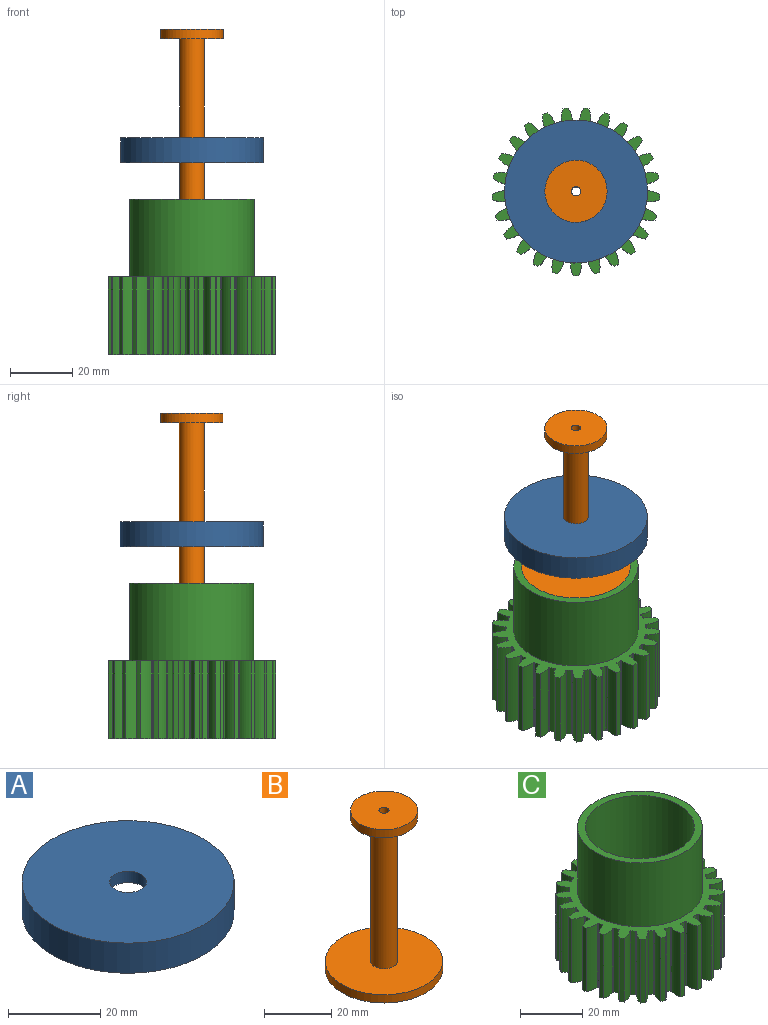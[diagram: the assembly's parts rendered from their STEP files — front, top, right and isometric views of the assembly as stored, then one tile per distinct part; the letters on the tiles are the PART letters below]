
ASSEMBLY  parts=3 mates=3
PART A: 6 faces, bbox 46x46x8 mm
  f0: cylinder r=4mm len=8mm, axis (0,0,1), area 75.4mm2, adj f1,f2
  f1: plane 40x40mm, normal (0,0,-1), area 1206.4mm2, adj f0,f3
  f2: plane 46x46mm, normal (0,0,1), area 1611.6mm2, adj f0,f4
  f3: cylinder r=20mm len=40mm, axis (0,0,1), area 628.3mm2, adj f1,f5
  f4: cylinder r=23mm len=46mm, axis (0,0,1), area 1156.1mm2, adj f2,f5
  f5: plane 46x46mm, normal (0,0,-1), area 405.3mm2, adj f3,f4
PART B: 8 faces, bbox 35x35x58 mm
  f0: cylinder r=17.5mm len=35mm, axis (0,0,-1), area 329.9mm2, adj f1,f2
  f1: plane 35x35mm, normal (0,0,1), area 911.8mm2, adj f0,f3
  f2: plane 35x35mm, normal (0,0,-1), area 955mm2, adj f0,f7
  f3: cylinder r=4mm len=52mm, axis (0,0,-1), area 1306.9mm2, adj f1,f6
  f4: cylinder r=10mm len=20mm, axis (0,0,-1), area 188.5mm2, adj f5,f6
  f5: plane 20x20mm, normal (0,0,1), area 307.1mm2, adj f4,f7
  f6: plane 20x20mm, normal (0,0,-1), area 263.9mm2, adj f3,f4
  f7: cylinder r=1.5mm len=58mm, axis (0,0,1), area 546.6mm2, adj f2,f5
PART C: 157 faces, bbox 54x53.9x50 mm
  f0: cylinder r=27mm len=25mm, axis (0,0,-1), area 41mm2, adj f24,f25,f33,f91
  f1: cylinder r=27mm len=25mm, axis (0,0,-1), area 41mm2, adj f24,f25,f94,f149
  f2: cylinder r=27mm len=25mm, axis (0,0,-1), area 41mm2, adj f24,f25,f86,f101
  f3: cylinder r=27mm len=25mm, axis (0,0,-1), area 41mm2, adj f24,f25,f99,f106
  f4: cylinder r=27mm len=25mm, axis (0,0,-1), area 41mm2, adj f24,f25,f81,f140
  f5: cylinder r=27mm len=25mm, axis (0,0,-1), area 41mm2, adj f24,f25,f73,f104
  f6: cylinder r=27mm len=25mm, axis (0,0,-1), area 41mm2, adj f24,f25,f76,f111
  f7: cylinder r=27mm len=25mm, axis (0,0,-1), area 41mm2, adj f24,f25,f68,f109
  f8: cylinder r=27mm len=25mm, axis (0,0,-1), area 41mm2, adj f24,f25,f71,f116
  f9: cylinder r=27mm len=25mm, axis (0,0,-1), area 41mm2, adj f24,f25,f63,f114
  f10: cylinder r=27mm len=25mm, axis (0,0,-1), area 41mm2, adj f24,f25,f66,f121
  f11: cylinder r=27mm len=25mm, axis (0,0,-1), area 41mm2, adj f24,f25,f58,f119
  f12: cylinder r=27mm len=25mm, axis (0,0,-1), area 41mm2, adj f24,f25,f61,f126
  f13: cylinder r=27mm len=25mm, axis (0,0,-1), area 41mm2, adj f24,f25,f53,f124
  f14: cylinder r=27mm len=25mm, axis (0,0,-1), area 41mm2, adj f24,f25,f56,f131
  f15: cylinder r=27mm len=25mm, axis (0,0,-1), area 41mm2, adj f24,f25,f48,f129
  f16: cylinder r=27mm len=25mm, axis (0,0,-1), area 41mm2, adj f24,f25,f51,f135
  f17: cylinder r=27mm len=25mm, axis (0,0,-1), area 41mm2, adj f24,f25,f43,f132
  f18: cylinder r=27mm len=25mm, axis (0,0,-1), area 41mm2, adj f24,f25,f46,f78
  f19: cylinder r=27mm len=25mm, axis (0,0,-1), area 41mm2, adj f24,f25,f38,f137
  f20: cylinder r=27mm len=25mm, axis (0,0,-1), area 41mm2, adj f24,f25,f41,f96
  f21: cylinder r=27mm len=25mm, axis (0,0,-1), area 41mm2, adj f24,f25,f88,f142
  f22: cylinder r=27mm len=25mm, axis (0,0,-1), area 41mm2, adj f24,f25,f35,f83
  f23: cylinder r=27mm len=25mm, axis (0,0,-1), area 41mm2, adj f24,f25,f29,f148
  f24: plane 53.97x53.88mm, normal (0,0,1), area 675.1mm2, adj f0,f1,f2,f3,f4,f5,f6,f7
  f25: plane 53.97x53.88mm, normal (0,0,-1), area 1912.1mm2, adj f0,f1,f2,f3,f4,f5,f6,f7
  f26: cylinder r=27mm len=25mm, axis (0,0,-1), area 41mm2, adj f24,f25,f28,f145
  f27: cylinder r=22.5mm len=25mm, axis (0,0,1), area 39.1mm2, adj f24,f25,f30,f31
  f28: cylinder r=8.41mm len=25mm, axis (0,0,1), area 110.6mm2, adj f24,f25,f26,f30
  f29: cylinder r=8.41mm len=25mm, axis (0,0,1), area 110.6mm2, adj f23,f24,f25,f31
  f30: cylinder r=0.3mm len=25mm, axis (0,0,-1), area 11.4mm2, adj f24,f25,f27,f28
  f31: cylinder r=0.3mm len=25mm, axis (0,0,-1), area 11.4mm2, adj f24,f25,f27,f29
  f32: cylinder r=0.3mm len=25mm, axis (0,0,-1), area 11.4mm2, adj f24,f25,f33,f36
  f33: cylinder r=8.41mm len=25mm, axis (0,0,1), area 110.6mm2, adj f0,f24,f25,f32
  f34: cylinder r=0.3mm len=25mm, axis (0,0,-1), area 11.4mm2, adj f24,f25,f35,f36
  f35: cylinder r=8.41mm len=25mm, axis (0,0,1), area 110.6mm2, adj f22,f24,f25,f34
  f36: cylinder r=22.5mm len=25mm, axis (0,0,1), area 39.1mm2, adj f24,f25,f32,f34
  f37: cylinder r=0.3mm len=25mm, axis (0,0,-1), area 11.4mm2, adj f24,f25,f38,f40
  f38: cylinder r=8.41mm len=25mm, axis (0,0,1), area 110.6mm2, adj f19,f24,f25,f37
  f39: cylinder r=0.3mm len=25mm, axis (0,0,-1), area 11.4mm2, adj f24,f25,f40,f41
  f40: cylinder r=22.5mm len=25mm, axis (0,0,1), area 39.1mm2, adj f24,f25,f37,f39
  f41: cylinder r=8.41mm len=25mm, axis (0,0,1), area 110.6mm2, adj f20,f24,f25,f39
  f42: cylinder r=0.3mm len=25mm, axis (0,0,-1), area 11.4mm2, adj f24,f25,f43,f45
  f43: cylinder r=8.41mm len=25mm, axis (0,0,1), area 110.6mm2, adj f17,f24,f25,f42
  f44: cylinder r=0.3mm len=25mm, axis (0,0,-1), area 11.4mm2, adj f24,f25,f45,f46
  f45: cylinder r=22.5mm len=25mm, axis (0,0,1), area 39.1mm2, adj f24,f25,f42,f44
  f46: cylinder r=8.41mm len=25mm, axis (0,0,1), area 110.6mm2, adj f18,f24,f25,f44
  f47: cylinder r=0.3mm len=25mm, axis (0,0,-1), area 11.4mm2, adj f24,f25,f48,f50
  f48: cylinder r=8.41mm len=25mm, axis (0,0,1), area 110.6mm2, adj f15,f24,f25,f47
  f49: cylinder r=0.3mm len=25mm, axis (0,0,-1), area 11.4mm2, adj f24,f25,f50,f51
  f50: cylinder r=22.5mm len=25mm, axis (0,0,1), area 39.1mm2, adj f24,f25,f47,f49
  f51: cylinder r=8.41mm len=25mm, axis (0,0,1), area 110.6mm2, adj f16,f24,f25,f49
  f52: cylinder r=0.3mm len=25mm, axis (0,0,-1), area 11.4mm2, adj f24,f25,f53,f55
  f53: cylinder r=8.41mm len=25mm, axis (0,0,1), area 110.6mm2, adj f13,f24,f25,f52
  f54: cylinder r=0.3mm len=25mm, axis (0,0,-1), area 11.4mm2, adj f24,f25,f55,f56
  f55: cylinder r=22.5mm len=25mm, axis (0,0,1), area 39.1mm2, adj f24,f25,f52,f54
  f56: cylinder r=8.41mm len=25mm, axis (0,0,1), area 110.6mm2, adj f14,f24,f25,f54
  f57: cylinder r=0.3mm len=25mm, axis (0,0,-1), area 11.4mm2, adj f24,f25,f58,f60
  f58: cylinder r=8.41mm len=25mm, axis (0,0,1), area 110.6mm2, adj f11,f24,f25,f57
  f59: cylinder r=0.3mm len=25mm, axis (0,0,-1), area 11.4mm2, adj f24,f25,f60,f61
  f60: cylinder r=22.5mm len=25mm, axis (0,0,1), area 39.1mm2, adj f24,f25,f57,f59
  f61: cylinder r=8.41mm len=25mm, axis (0,0,1), area 110.6mm2, adj f12,f24,f25,f59
  f62: cylinder r=0.3mm len=25mm, axis (0,0,-1), area 11.4mm2, adj f24,f25,f63,f65
  f63: cylinder r=8.41mm len=25mm, axis (0,0,1), area 110.6mm2, adj f9,f24,f25,f62
  f64: cylinder r=0.3mm len=25mm, axis (0,0,-1), area 11.4mm2, adj f24,f25,f65,f66
  f65: cylinder r=22.5mm len=25mm, axis (0,0,1), area 39.1mm2, adj f24,f25,f62,f64
  f66: cylinder r=8.41mm len=25mm, axis (0,0,1), area 110.6mm2, adj f10,f24,f25,f64
  f67: cylinder r=0.3mm len=25mm, axis (0,0,-1), area 11.4mm2, adj f24,f25,f68,f70
  f68: cylinder r=8.41mm len=25mm, axis (0,0,1), area 110.6mm2, adj f7,f24,f25,f67
  f69: cylinder r=0.3mm len=25mm, axis (0,0,-1), area 11.4mm2, adj f24,f25,f70,f71
  f70: cylinder r=22.5mm len=25mm, axis (0,0,1), area 39.1mm2, adj f24,f25,f67,f69
  f71: cylinder r=8.41mm len=25mm, axis (0,0,1), area 110.6mm2, adj f8,f24,f25,f69
  f72: cylinder r=0.3mm len=25mm, axis (0,0,-1), area 11.4mm2, adj f24,f25,f73,f75
  f73: cylinder r=8.41mm len=25mm, axis (0,0,1), area 110.6mm2, adj f5,f24,f25,f72
  f74: cylinder r=0.3mm len=25mm, axis (0,0,-1), area 11.4mm2, adj f24,f25,f75,f76
  f75: cylinder r=22.5mm len=25mm, axis (0,0,1), area 39.1mm2, adj f24,f25,f72,f74
  f76: cylinder r=8.41mm len=25mm, axis (0,0,1), area 110.6mm2, adj f6,f24,f25,f74
  f77: cylinder r=0.3mm len=25mm, axis (0,0,-1), area 11.4mm2, adj f24,f25,f78,f80
  f78: cylinder r=8.41mm len=25mm, axis (0,0,1), area 110.6mm2, adj f18,f24,f25,f77
  f79: cylinder r=0.3mm len=25mm, axis (0,0,-1), area 11.4mm2, adj f24,f25,f80,f81
  f80: cylinder r=22.5mm len=25mm, axis (0,0,1), area 39.1mm2, adj f24,f25,f77,f79
  f81: cylinder r=8.41mm len=25mm, axis (0,0,1), area 110.6mm2, adj f4,f24,f25,f79
  f82: cylinder r=0.3mm len=25mm, axis (0,0,-1), area 11.4mm2, adj f24,f25,f83,f85
  f83: cylinder r=8.41mm len=25mm, axis (0,0,1), area 110.6mm2, adj f22,f24,f25,f82
  f84: cylinder r=0.3mm len=25mm, axis (0,0,-1), area 11.4mm2, adj f24,f25,f85,f86
  f85: cylinder r=22.5mm len=25mm, axis (0,0,1), area 39.1mm2, adj f24,f25,f82,f84
  f86: cylinder r=8.41mm len=25mm, axis (0,0,1), area 110.6mm2, adj f2,f24,f25,f84
  f87: cylinder r=0.3mm len=25mm, axis (0,0,-1), area 11.4mm2, adj f24,f25,f88,f90
  f88: cylinder r=8.41mm len=25mm, axis (0,0,1), area 110.6mm2, adj f21,f24,f25,f87
  f89: cylinder r=0.3mm len=25mm, axis (0,0,-1), area 11.4mm2, adj f24,f25,f90,f91
  f90: cylinder r=22.5mm len=25mm, axis (0,0,1), area 39.1mm2, adj f24,f25,f87,f89
  f91: cylinder r=8.41mm len=25mm, axis (0,0,1), area 110.6mm2, adj f0,f24,f25,f89
  f92: cylinder r=22.5mm len=25mm, axis (0,0,1), area 39.1mm2, adj f24,f25,f93,f95
  f93: cylinder r=0.3mm len=25mm, axis (0,0,-1), area 11.4mm2, adj f24,f25,f92,f94
  f94: cylinder r=8.41mm len=25mm, axis (0,0,1), area 110.6mm2, adj f1,f24,f25,f93
  f95: cylinder r=0.3mm len=25mm, axis (0,0,-1), area 11.4mm2, adj f24,f25,f92,f96
  f96: cylinder r=8.41mm len=25mm, axis (0,0,1), area 110.6mm2, adj f20,f24,f25,f95
  f97: cylinder r=22.5mm len=25mm, axis (0,0,1), area 39.1mm2, adj f24,f25,f98,f100
  f98: cylinder r=0.3mm len=25mm, axis (0,0,-1), area 11.4mm2, adj f24,f25,f97,f99
  f99: cylinder r=8.41mm len=25mm, axis (0,0,1), area 110.6mm2, adj f3,f24,f25,f98
  f100: cylinder r=0.3mm len=25mm, axis (0,0,-1), area 11.4mm2, adj f24,f25,f97,f101
  f101: cylinder r=8.41mm len=25mm, axis (0,0,1), area 110.6mm2, adj f2,f24,f25,f100
  f102: cylinder r=22.5mm len=25mm, axis (0,0,1), area 39.1mm2, adj f24,f25,f103,f105
  f103: cylinder r=0.3mm len=25mm, axis (0,0,-1), area 11.4mm2, adj f24,f25,f102,f104
  f104: cylinder r=8.41mm len=25mm, axis (0,0,1), area 110.6mm2, adj f5,f24,f25,f103
  f105: cylinder r=0.3mm len=25mm, axis (0,0,-1), area 11.4mm2, adj f24,f25,f102,f106
  f106: cylinder r=8.41mm len=25mm, axis (0,0,1), area 110.6mm2, adj f3,f24,f25,f105
  f107: cylinder r=22.5mm len=25mm, axis (0,0,1), area 39.1mm2, adj f24,f25,f108,f110
  f108: cylinder r=0.3mm len=25mm, axis (0,0,-1), area 11.4mm2, adj f24,f25,f107,f109
  f109: cylinder r=8.41mm len=25mm, axis (0,0,1), area 110.6mm2, adj f7,f24,f25,f108
  f110: cylinder r=0.3mm len=25mm, axis (0,0,-1), area 11.4mm2, adj f24,f25,f107,f111
  f111: cylinder r=8.41mm len=25mm, axis (0,0,1), area 110.6mm2, adj f6,f24,f25,f110
  f112: cylinder r=22.5mm len=25mm, axis (0,0,1), area 39.1mm2, adj f24,f25,f113,f115
  f113: cylinder r=0.3mm len=25mm, axis (0,0,-1), area 11.4mm2, adj f24,f25,f112,f114
  f114: cylinder r=8.41mm len=25mm, axis (0,0,1), area 110.6mm2, adj f9,f24,f25,f113
  f115: cylinder r=0.3mm len=25mm, axis (0,0,-1), area 11.4mm2, adj f24,f25,f112,f116
  f116: cylinder r=8.41mm len=25mm, axis (0,0,1), area 110.6mm2, adj f8,f24,f25,f115
  f117: cylinder r=22.5mm len=25mm, axis (0,0,1), area 39.1mm2, adj f24,f25,f118,f120
  f118: cylinder r=0.3mm len=25mm, axis (0,0,-1), area 11.4mm2, adj f24,f25,f117,f119
  f119: cylinder r=8.41mm len=25mm, axis (0,0,1), area 110.6mm2, adj f11,f24,f25,f118
  f120: cylinder r=0.3mm len=25mm, axis (0,0,-1), area 11.4mm2, adj f24,f25,f117,f121
  f121: cylinder r=8.41mm len=25mm, axis (0,0,1), area 110.6mm2, adj f10,f24,f25,f120
  f122: cylinder r=22.5mm len=25mm, axis (0,0,1), area 39.1mm2, adj f24,f25,f123,f125
  f123: cylinder r=0.3mm len=25mm, axis (0,0,-1), area 11.4mm2, adj f24,f25,f122,f124
  f124: cylinder r=8.41mm len=25mm, axis (0,0,1), area 110.6mm2, adj f13,f24,f25,f123
  f125: cylinder r=0.3mm len=25mm, axis (0,0,-1), area 11.4mm2, adj f24,f25,f122,f126
  f126: cylinder r=8.41mm len=25mm, axis (0,0,1), area 110.6mm2, adj f12,f24,f25,f125
  f127: cylinder r=22.5mm len=25mm, axis (0,0,1), area 39.1mm2, adj f24,f25,f128,f130
  f128: cylinder r=0.3mm len=25mm, axis (0,0,-1), area 11.4mm2, adj f24,f25,f127,f129
  f129: cylinder r=8.41mm len=25mm, axis (0,0,1), area 110.6mm2, adj f15,f24,f25,f128
  f130: cylinder r=0.3mm len=25mm, axis (0,0,-1), area 11.4mm2, adj f24,f25,f127,f131
  f131: cylinder r=8.41mm len=25mm, axis (0,0,1), area 110.6mm2, adj f14,f24,f25,f130
  f132: cylinder r=8.41mm len=25mm, axis (0,0,1), area 110.6mm2, adj f17,f24,f25,f134
  f133: cylinder r=22.5mm len=25mm, axis (0,0,1), area 39.1mm2, adj f24,f25,f134,f136
  f134: cylinder r=0.3mm len=25mm, axis (0,0,-1), area 11.4mm2, adj f24,f25,f132,f133
  f135: cylinder r=8.41mm len=25mm, axis (0,0,1), area 110.6mm2, adj f16,f24,f25,f136
  f136: cylinder r=0.3mm len=25mm, axis (0,0,-1), area 11.4mm2, adj f24,f25,f133,f135
  f137: cylinder r=8.41mm len=25mm, axis (0,0,1), area 110.6mm2, adj f19,f24,f25,f139
  f138: cylinder r=22.5mm len=25mm, axis (0,0,1), area 39.1mm2, adj f24,f25,f139,f141
  f139: cylinder r=0.3mm len=25mm, axis (0,0,-1), area 11.4mm2, adj f24,f25,f137,f138
  f140: cylinder r=8.41mm len=25mm, axis (0,0,1), area 110.6mm2, adj f4,f24,f25,f141
  f141: cylinder r=0.3mm len=25mm, axis (0,0,-1), area 11.4mm2, adj f24,f25,f138,f140
  f142: cylinder r=8.41mm len=25mm, axis (0,0,1), area 110.6mm2, adj f21,f24,f25,f144
  f143: cylinder r=22.5mm len=25mm, axis (0,0,1), area 39.1mm2, adj f24,f25,f144,f146
  f144: cylinder r=0.3mm len=25mm, axis (0,0,-1), area 11.4mm2, adj f24,f25,f142,f143
  f145: cylinder r=8.41mm len=25mm, axis (0,0,1), area 110.6mm2, adj f24,f25,f26,f146
  f146: cylinder r=0.3mm len=25mm, axis (0,0,-1), area 11.4mm2, adj f24,f25,f143,f145
  f147: cylinder r=22.5mm len=25mm, axis (0,0,1), area 39.1mm2, adj f24,f25,f150,f151
  f148: cylinder r=8.41mm len=25mm, axis (0,0,1), area 110.6mm2, adj f23,f24,f25,f150
  f149: cylinder r=8.41mm len=25mm, axis (0,0,1), area 110.6mm2, adj f1,f24,f25,f151
  f150: cylinder r=0.3mm len=25mm, axis (0,0,-1), area 11.4mm2, adj f24,f25,f147,f148
  f151: cylinder r=0.3mm len=25mm, axis (0,0,-1), area 11.4mm2, adj f24,f25,f147,f149
  f152: cylinder r=17.5mm len=47.5mm, axis (0,0,-1), area 5222.9mm2, adj f154,f155
  f153: cylinder r=20mm len=40mm, axis (0,0,-1), area 3141.6mm2, adj f24,f154
  f154: plane 40x40mm, normal (0,0,1), area 294.5mm2, adj f152,f153
  f155: plane 35x35mm, normal (0,0,1), area 942.5mm2, adj f152,f156
  f156: cylinder r=2.5mm len=5mm, axis (0,0,1), area 39.3mm2, adj f25,f155
PLACE A t=(0,0,69.69)mm
PLACE B t=(0,0,46.58)mm
PLACE C t=(0,0,12.5)mm
MATE slider B.f0 <-> C.f0  axis (0,0,-1) through (0,0,46.58)mm
MATE slider A.f0 <-> B.f0  axis (0,0,-1) through (0,0,66.69)mm
MATE slider A.f0 <-> C.f0  axis (0,0,-1) through (0,0,66.69)mm
